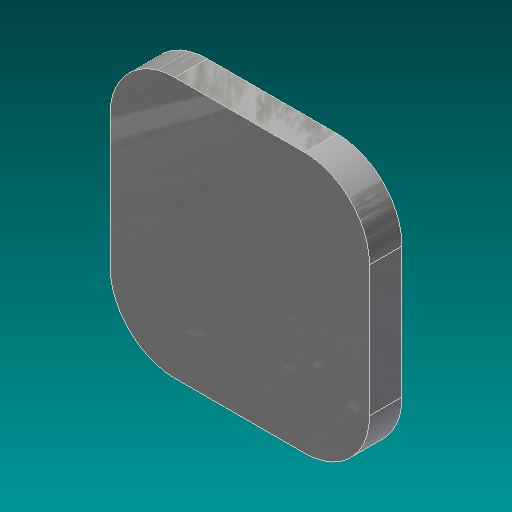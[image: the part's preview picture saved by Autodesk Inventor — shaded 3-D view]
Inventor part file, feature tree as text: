
AUTODESK INVENTOR PART (.ipt)
format: ipt  version: 2017 (Build 210142000, 142)  size: 125,952 bytes
history: native  units: in
note: dims shown in document units (in); Inventor stores cm internally (conversion verified against a paired STEP export)
features: extrude x1, sketch x1
ambient origin geometry x8: Origin, YZ Plane, XZ Plane, XY Plane, X Axis, Y Axis, Z Axis, Center Point
bodies: Solid1 (feature_tree)
feature tree (2):
  extrude  "Extrusion1"  Depth=2.0076in
  sketch  "Sketch1"  dims[d0=2.0in d1=2.0076in d2=0.5in d3=0.25in d4=0.0in]
